FCSTD DOCUMENT  (FreeCAD 0.21R33771 (Git))
Label: master_kumiko_box
License: All rights reserved
LicenseURL: https://en.wikipedia.org/wiki/All_rights_reserved
objects: App::Link×3, App::Part×2, Spreadsheet::Sheet×1
EXTERNAL_REF file=assembly/box_assembly.FCStd obj=Part
EXTERNAL_REF file=assembly/lid_assembly.FCStd obj=Part
EXTERNAL_REF file=assembly/kumiko_assembly.FCStd obj=Part001

FEATURE [Spreadsheet::Sheet] Spreadsheet  label="SpreadSheet"
  cells = A1='name; B1='value; C1='calc (y/n); A2='box_length; B2(box_length)=130; C2='n; A3='box_width; B3(box_width)==B2 / 2 + B5 - B13 / 2; C3='n; A4='box_height; B4(box_height)=60; C4='y; A5='box_thickness; B5(box_thickness)=11.5; C5='y; A7='lid_height; B7(lid_height)==B8 * 17 / 8.5; C7='y; A8='lid_frame_width; B8(lid_frame_width)==B5 - B13; C8='y; A9='lid_lip_width; B9(lid_lip_width)==B5 - B8; C9='y; A10='lid_lip_height; B10(lid_lip_hight)=3; C10='y; A12='kumiko_hight; B12(kumiko_hight)==B7 * 11 / 17; C12='y; A13='kumiko_thickness; B13(kumiko_thickness)=3; C13='n; A14='kumiko_grid_size; B14(kumiko_grid_size)==(B2 - 2 * B8 - B13) / 4; C14='y; A16='box_wall_height; B16(box_wall_height)==B4 - B7 - B18; C16='y; A18='floor_edge; B18(floor_edge)=2; C18='n; A20='cnc_spacing; B20(cnc_spacing)=0; C20='y
FEATURE [App::Link] Link  label="box"
  LinkedObject = -> <external assembly/box_assembly.FCStd>#Part
FEATURE [App::Link] Link001  label="lid"
  LinkPlacement = pos=(0,0,43) rot=(0,0,1;0rad)
  LinkedObject = -> <external assembly/lid_assembly.FCStd>#Part
  Placement = pos=(0,0,43) rot=(0,0,1;0rad)
  expr: .Placement.Base.z = <<SpreadSheet>>.box_height - <<SpreadSheet>>.lid_height
FEATURE [App::Link] Link002  label="kumiko_assembly"
  LinkPlacement = pos=(8.5,8.5,49) rot=(0,0,1;0rad)
  LinkedObject = -> <external assembly/kumiko_assembly.FCStd>#Part001
  Placement = pos=(8.5,8.5,49) rot=(0,0,1;0rad)
  expr: .Placement.Base.x = <<SpreadSheet>>.lid_frame_width
  expr: .Placement.Base.y = <<SpreadSheet>>.lid_frame_width
  expr: .Placement.Base.z = <<SpreadSheet>>.box_height - Spreadsheet.kumiko_hight
FEATURE [App::Part] Part  label="lid_complete"
  Group = -> [Link002,Link001]
  Origin = -> Origin
FEATURE [App::Part] Part001  label="kumiko_box_complete"
  Group = -> [Part,Link]
  Origin = -> Origin001

RESOLVED EXTERNAL PARTS (link-assembly join: the EXTERNAL_REF files above that resolve inside this repo's crawl, each included once):
---- part assembly/box_assembly.FCStd = doc fcstd_d9ec08d89ce1 ----
FCSTD DOCUMENT  (FreeCAD 0.21R33694 (Git))
Label: box_assembly
License: All rights reserved
LicenseURL: http://en.wikipedia.org/wiki/All_rights_reserved
objects: App::Link×14, App::Part×1
EXTERNAL_REF file=../master_kumiko_box.FCStd obj=Spreadsheet
EXTERNAL_REF file=../parts/box/kumiko_box_floor.FCStd obj=Body032
EXTERNAL_REF file=../parts/box/kumiko_box_wall_long.FCStd obj=Body009
EXTERNAL_REF file=../parts/box/kumiko_box_wall_short.FCStd obj=Body009
EXTERNAL_REF file=../parts/box/kumiko_box_key_miter.FCStd obj=Body014

FEATURE [App::Link] Link  label="SpreadSheet"
  LinkedObject = -> <external ../master_kumiko_box.FCStd>#Spreadsheet
FEATURE [App::Link] Link001  label="floor"
  LinkPlacement = pos=(5.75,5.75,0) rot=(0,0,1;0rad)
  LinkedObject = -> <external ../parts/box/kumiko_box_floor.FCStd>#Body032
  Placement = pos=(5.75,5.75,0) rot=(0,0,1;0rad)
  expr: .Placement.Base.x = <<SpreadSheet>>.box_thickness / 2
  expr: .Placement.Base.y = <<SpreadSheet>>.box_thickness / 2
FEATURE [App::Link] Link002  label="wall_front"
  LinkPlacement = pos=(130,0,2) rot=(0,0,1;1.5708rad)
  LinkedObject = -> <external ../parts/box/kumiko_box_wall_long.FCStd>#Body009
  Placement = pos=(130,0,2) rot=(0,0,1;1.5708rad)
  expr: .Placement.Base.x = <<SpreadSheet>>.box_length
  expr: .Placement.Base.z = <<SpreadSheet>>.floor_edge
  expr: .Placement.Rotation.Angle = 90
FEATURE [App::Link] Link003  label="wall_left"
  LinkPlacement = pos=(0,0,2) rot=(0,0,1;0rad)
  LinkedObject = -> <external ../parts/box/kumiko_box_wall_short.FCStd>#Body009
  Placement = pos=(0,0,2) rot=(0,0,1;0rad)
  expr: .Placement.Base.x = 0
  expr: .Placement.Base.y = 0
  expr: .Placement.Base.z = <<SpreadSheet>>.floor_edge
FEATURE [App::Link] Link004  label="wall_back"
  LinkPlacement = pos=(0,75,2) rot=(0,0,1;4.71239rad)
  LinkedObject = -> <external ../parts/box/kumiko_box_wall_long.FCStd>#Body009
  Placement = pos=(0,75,2) rot=(0,0,1;4.71239rad)
  expr: .Placement.Base.x = 0
  expr: .Placement.Base.y = <<SpreadSheet>>.box_width
  expr: .Placement.Base.z = <<SpreadSheet>>.floor_edge
  expr: .Placement.Rotation.Angle = 270
FEATURE [App::Link] Link005  label="wall_right"
  LinkPlacement = pos=(130,75,2) rot=(0,0,1;3.14159rad)
  LinkedObject = -> <external ../parts/box/kumiko_box_wall_short.FCStd>#Body009
  Placement = pos=(130,75,2) rot=(0,0,1;3.14159rad)
  expr: .Placement.Base.x = <<SpreadSheet>>.box_length
  expr: .Placement.Base.y = <<SpreadSheet>>.box_width
  expr: .Placement.Base.z = <<SpreadSheet>>.floor_edge
  expr: .Placement.Rotation.Angle = 180
FEATURE [App::Link] Link006  label="miter_key_a"
  LinkPlacement = pos=(0,0,9) rot=(0,0,1;0rad)
  LinkedObject = -> <external ../parts/box/kumiko_box_key_miter.FCStd>#Body014
  Placement = pos=(0,0,9) rot=(0,0,1;0rad)
  expr: .Placement.Base.x = 0
  expr: .Placement.Base.z = <<SpreadSheet>>.floor_edge + (<<SpreadSheet>>.lid_height - <<SpreadSheet>>.kumiko_thickness) / 2
FEATURE [App::Link] Link007  label="miter_key_b"
  LinkPlacement = pos=(0,0,33) rot=(0,0,1;0rad)
  LinkedObject = -> <external ../parts/box/kumiko_box_key_miter.FCStd>#Body014
  Placement = pos=(0,0,33) rot=(0,0,1;0rad)
  expr: .Placement.Base.z = <<SpreadSheet>>.box_height - <<SpreadSheet>>.lid_height - (<<SpreadSheet>>.lid_height + <<SpreadSheet>>.kumiko_thickness) / 2
FEATURE [App::Link] Link008  label="miter_key_c"
  LinkPlacement = pos=(130,0,9) rot=(0,0,1;1.5708rad)
  LinkedObject = -> <external ../parts/box/kumiko_box_key_miter.FCStd>#Body014
  Placement = pos=(130,0,9) rot=(0,0,1;1.5708rad)
  expr: .Placement.Base.x = <<SpreadSheet>>.box_length
  expr: .Placement.Base.z = <<SpreadSheet>>.floor_edge + (<<SpreadSheet>>.lid_height - <<SpreadSheet>>.kumiko_thickness) / 2
  expr: .Placement.Rotation.Angle = 90
FEATURE [App::Link] Link009  label="miter_key_d"
  LinkPlacement = pos=(130,0,33) rot=(0,0,1;1.5708rad)
  LinkedObject = -> <external ../parts/box/kumiko_box_key_miter.FCStd>#Body014
  Placement = pos=(130,0,33) rot=(0,0,1;1.5708rad)
  expr: .Placement.Base.x = <<SpreadSheet>>.box_length
  expr: .Placement.Base.z = <<SpreadSheet>>.box_height - <<SpreadSheet>>.lid_height - (<<SpreadSheet>>.lid_height + <<SpreadSheet>>.kumiko_thickness) / 2
  expr: .Placement.Rotation.Angle = 90
FEATURE [App::Link] Link010  label="miter_key_e"
  LinkPlacement = pos=(130,75,9) rot=(0,0,1;3.14159rad)
  LinkedObject = -> <external ../parts/box/kumiko_box_key_miter.FCStd>#Body014
  Placement = pos=(130,75,9) rot=(0,0,1;3.14159rad)
  expr: .Placement.Base.x = <<SpreadSheet>>.box_length
  expr: .Placement.Base.y = <<SpreadSheet>>.box_width
  expr: .Placement.Base.z = <<SpreadSheet>>.floor_edge + (<<SpreadSheet>>.lid_height - <<SpreadSheet>>.kumiko_thickness) / 2
FEATURE [App::Link] Link011  label="miter_key_f"
  LinkPlacement = pos=(130,75,33) rot=(0,0,1;3.14159rad)
  LinkedObject = -> <external ../parts/box/kumiko_box_key_miter.FCStd>#Body014
  Placement = pos=(130,75,33) rot=(0,0,1;3.14159rad)
  expr: .Placement.Base.x = <<SpreadSheet>>.box_length
  expr: .Placement.Base.y = <<SpreadSheet>>.box_width
  expr: .Placement.Base.z = <<SpreadSheet>>.box_height - <<SpreadSheet>>.lid_height - (<<SpreadSheet>>.lid_height + <<SpreadSheet>>.kumiko_thickness) / 2
FEATURE [App::Link] Link012  label="miter_key_g"
  LinkPlacement = pos=(0,75,9) rot=(0,0,1;4.71239rad)
  LinkedObject = -> <external ../parts/box/kumiko_box_key_miter.FCStd>#Body014
  Placement = pos=(0,75,9) rot=(0,0,1;4.71239rad)
  expr: .Placement.Base.y = <<SpreadSheet>>.box_width
  expr: .Placement.Base.z = <<SpreadSheet>>.floor_edge + (<<SpreadSheet>>.lid_height - <<SpreadSheet>>.kumiko_thickness) / 2
FEATURE [App::Link] Link013  label="miter_key_h"
  LinkPlacement = pos=(0,75,33) rot=(0,0,1;4.71239rad)
  LinkedObject = -> <external ../parts/box/kumiko_box_key_miter.FCStd>#Body014
  Placement = pos=(0,75,33) rot=(0,0,1;4.71239rad)
  expr: .Placement.Base.y = <<SpreadSheet>>.box_width
  expr: .Placement.Base.z = <<SpreadSheet>>.box_height - <<SpreadSheet>>.lid_height - (<<SpreadSheet>>.lid_height + <<SpreadSheet>>.kumiko_thickness) / 2
FEATURE [App::Part] Part  label="box"
  Group = -> [Link001,Link004,Link003,Link006,Link007,Link008,Link005,Link002,Link009,Link010,Link011,Link012,Link013]
  Origin = -> Origin
---- part assembly/kumiko_assembly.FCStd = doc fcstd_e2ea94e172d7 ----
FCSTD DOCUMENT  (FreeCAD 0.21R33694 (Git))
Label: kumiko_assembly
License: All rights reserved
LicenseURL: http://en.wikipedia.org/wiki/All_rights_reserved
objects: App::Link×7, App::Part×2
EXTERNAL_REF file=../master_kumiko_box.FCStd obj=Spreadsheet
EXTERNAL_REF file=kumiko_lattice_assembly.FCStd obj=Part
EXTERNAL_REF file=asanoha_assembly.FCStd obj=Part001

FEATURE [App::Link] Link  label="SpreadSheet"
  LinkedObject = -> <external ../master_kumiko_box.FCStd>#Spreadsheet
FEATURE [App::Link] Link001  label="lattice"
  LinkedObject = -> <external kumiko_lattice_assembly.FCStd>#Part
FEATURE [App::Link] Link002  label="asanoha_left_bottom"
  LinkPlacement = pos=(3,3,0) rot=(0,0,1;0rad)
  LinkedObject = -> <external asanoha_assembly.FCStd>#Part001
  Placement = pos=(3,3,0) rot=(0,0,1;0rad)
  expr: .Placement.Base.x = <<SpreadSheet>>.kumiko_thickness
  expr: .Placement.Base.y = <<SpreadSheet>>.kumiko_thickness
FEATURE [App::Link] Link003  label="asanoha_left_top"
  LinkPlacement = pos=(3,55,0) rot=(0,0,1;4.71239rad)
  LinkedObject = -> <external asanoha_assembly.FCStd>#Part001
  Placement = pos=(3,55,0) rot=(0,0,1;4.71239rad)
  expr: .Placement.Base.x = <<SpreadSheet>>.kumiko_thickness
  expr: .Placement.Base.y = 2 * <<SpreadSheet>>.kumiko_grid_size
  expr: .Placement.Base.z = 0
FEATURE [App::Link] Link004  label="asanoha_right_bottom"
  LinkPlacement = pos=(55,3,0) rot=(0,0,1;1.5708rad)
  LinkedObject = -> Link002
  Placement = pos=(55,3,0) rot=(0,0,1;1.5708rad)
  expr: .Placement.Base.x = 2 * <<SpreadSheet>>.kumiko_grid_size
  expr: .Placement.Base.y = <<SpreadSheet>>.kumiko_thickness
FEATURE [App::Link] Link005  label="asanoha_right_top"
  LinkPlacement = pos=(30.5,30.5,0) rot=(0,0,1;0rad)
  LinkedObject = -> Link002
  Placement = pos=(30.5,30.5,0) rot=(0,0,1;0rad)
  expr: .Placement.Base.x = <<SpreadSheet>>.kumiko_grid_size + <<SpreadSheet>>.kumiko_thickness
  expr: .Placement.Base.y = <<SpreadSheet>>.kumiko_grid_size + <<SpreadSheet>>.kumiko_thickness
FEATURE [App::Part] Part  label="asanoha_left"
  Group = -> [Link004,Link005,Link003,Link002]
  Origin = -> Origin
FEATURE [App::Link] Link006  label="asanoha_right"
  LinkPlacement = pos=(55,0,0) rot=(0,0,1;0rad)
  LinkedObject = -> Part
  Placement = pos=(55,0,0) rot=(0,0,1;0rad)
  expr: .Placement.Base.x = 2 * <<SpreadSheet>>.kumiko_grid_size
FEATURE [App::Part] Part001  label="kumiko_assembly"
  Group = -> [Link006,Part,Link001]
  Origin = -> Origin001
---- part assembly/lid_assembly.FCStd = doc fcstd_dfe8505de392 ----
FCSTD DOCUMENT  (FreeCAD 0.21R33694 (Git))
Label: lid_assembly
License: All rights reserved
LicenseURL: http://en.wikipedia.org/wiki/All_rights_reserved
objects: App::Link×9, App::Part×1
EXTERNAL_REF file=../master_kumiko_box.FCStd obj=Spreadsheet
EXTERNAL_REF file=../parts/box/kumiko_lid_long.FCStd obj=Body001
EXTERNAL_REF file=../parts/box/kumiko_lid_short.FCStd obj=Body001
EXTERNAL_REF file=../parts/box/kumiko_box_key_miter.FCStd obj=Body014

FEATURE [App::Link] Link  label="SpreadSheet"
  LinkedObject = -> <external ../master_kumiko_box.FCStd>#Spreadsheet
FEATURE [App::Link] Link001  label="lid_front"
  LinkPlacement = pos=(0,0,0) rot=(0,0,1;1.5708rad)
  LinkedObject = -> <external ../parts/box/kumiko_lid_long.FCStd>#Body001
  Placement = pos=(0,0,0) rot=(0,0,1;1.5708rad)
  expr: .Placement.Base.x = 0
FEATURE [App::Link] Link002  label="lid_left"
  LinkPlacement = pos=(0,75,0) rot=(0,0,1;0rad)
  LinkedObject = -> <external ../parts/box/kumiko_lid_short.FCStd>#Body001
  Placement = pos=(0,75,0) rot=(0,0,1;0rad)
  expr: .Placement.Base.y = <<SpreadSheet>>.box_width
FEATURE [App::Link] Link003  label="lid_back"
  LinkPlacement = pos=(130,75,0) rot=(0,0,1;4.71239rad)
  LinkedObject = -> <external ../parts/box/kumiko_lid_long.FCStd>#Body001
  Placement = pos=(130,75,0) rot=(0,0,1;4.71239rad)
  expr: .Placement.Base.x = <<SpreadSheet>>.box_length
  expr: .Placement.Base.y = <<SpreadSheet>>.box_width
FEATURE [App::Link] Link004  label="lid_side"
  LinkPlacement = pos=(130,0,0) rot=(0,0,1;3.14159rad)
  LinkedObject = -> <external ../parts/box/kumiko_lid_short.FCStd>#Body001
  Placement = pos=(130,0,0) rot=(0,0,1;3.14159rad)
  expr: .Placement.Base.x = <<SpreadSheet>>.box_length
  expr: .Placement.Rotation.Angle = 180
FEATURE [App::Link] Link005  label="miter_key_a"
  LinkPlacement = pos=(0,0,7) rot=(0,0,1;0rad)
  LinkedObject = -> <external ../parts/box/kumiko_box_key_miter.FCStd>#Body014
  Placement = pos=(0,0,7) rot=(0,0,1;0rad)
  expr: .Placement.Base.z = (<<SpreadSheet>>.lid_height - <<SpreadSheet>>.kumiko_thickness) / 2
FEATURE [App::Link] Link006  label="miter_key_b"
  LinkPlacement = pos=(130,0,7) rot=(0,0,1;1.5708rad)
  LinkedObject = -> <external ../parts/box/kumiko_box_key_miter.FCStd>#Body014
  Placement = pos=(130,0,7) rot=(0,0,1;1.5708rad)
  expr: .Placement.Base.x = <<SpreadSheet>>.box_length
  expr: .Placement.Base.z = (<<SpreadSheet>>.lid_height - <<SpreadSheet>>.kumiko_thickness) / 2
  expr: .Placement.Rotation.Angle = 90
FEATURE [App::Link] Link007  label="miter_key_c"
  LinkPlacement = pos=(130,75,7) rot=(0,0,1;3.14159rad)
  LinkedObject = -> <external ../parts/box/kumiko_box_key_miter.FCStd>#Body014
  Placement = pos=(130,75,7) rot=(0,0,1;3.14159rad)
  expr: .Placement.Base.x = <<SpreadSheet>>.box_length
  expr: .Placement.Base.y = <<SpreadSheet>>.box_width
  expr: .Placement.Base.z = (<<SpreadSheet>>.lid_height - <<SpreadSheet>>.kumiko_thickness) / 2
FEATURE [App::Link] Link008  label="miter_key_d"
  LinkPlacement = pos=(0,75,7) rot=(0,0,1;4.71239rad)
  LinkedObject = -> <external ../parts/box/kumiko_box_key_miter.FCStd>#Body014
  Placement = pos=(0,75,7) rot=(0,0,1;4.71239rad)
  expr: .Placement.Base.y = <<SpreadSheet>>.box_width
  expr: .Placement.Base.z = (<<SpreadSheet>>.lid_height - <<SpreadSheet>>.kumiko_thickness) / 2
  expr: .Placement.Rotation.Angle = 270
FEATURE [App::Part] Part  label="lid"
  Group = -> [Link004,Link003,Link002,Link001,Link005,Link006,Link007,Link008]
  Origin = -> Origin
